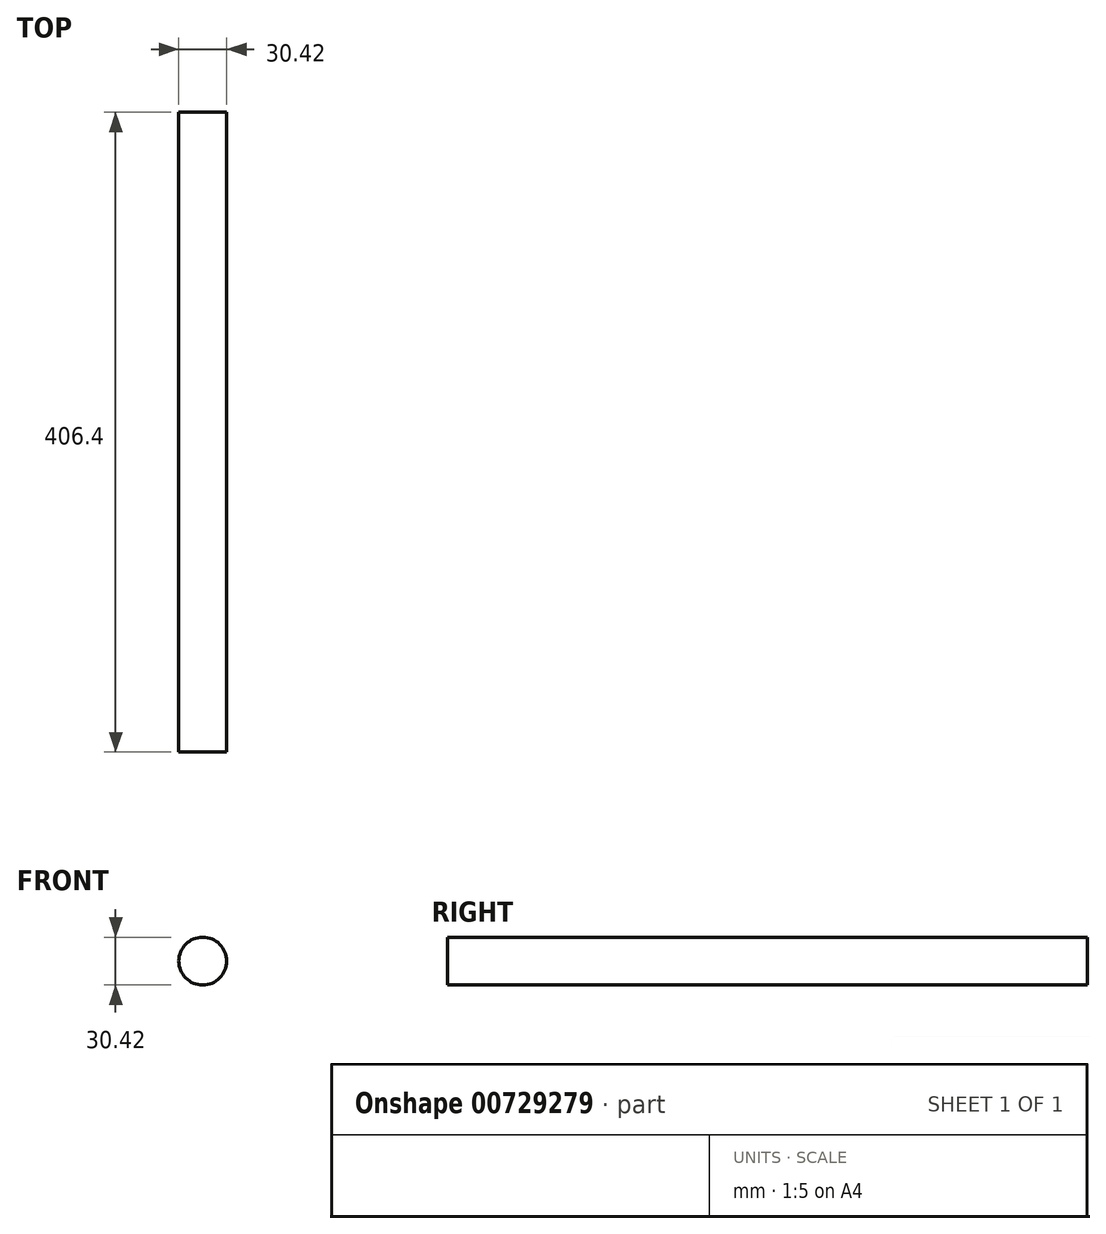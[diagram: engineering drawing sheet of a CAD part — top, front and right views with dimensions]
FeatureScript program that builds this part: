
annotation { "Feature Type Name" : "Feature", "Feature Type Description" : "" }
export const myFeature = defineFeature(function(context is Context, id is Id, definition is map)
    precondition{}
    {
        {
            var Q0;
            Q0=qCreatedBy(makeId("Front.planeOp"),FACE);
            var sketch = newSketch(context, id + "F0", { "sketchPlane" : qUnion([Q0])});
            skCircle(sketch, "E0", {"center": v(0, 0) * mm, "radius": 15.2 * mm});
            skSolve(sketch);
        }
        {
            var Q0;
            Q0=makeQuery(id+"F0.imprint","IMPRINT",FACE,{"disambiguationData":[TD([[makeQuery(id+"F0.imprint","IMPRINT",EDGE,{"derivedFrom":sQuery(id+"F0.wireOp",EDGE,"E0")}),1.0]])]});
            extrude(context, id + "F1", {"entities" : qUnion([Q0]), "depth" : 406.4 * mm, "offsetDistance" : 25.4 * mm});
        }
    });
